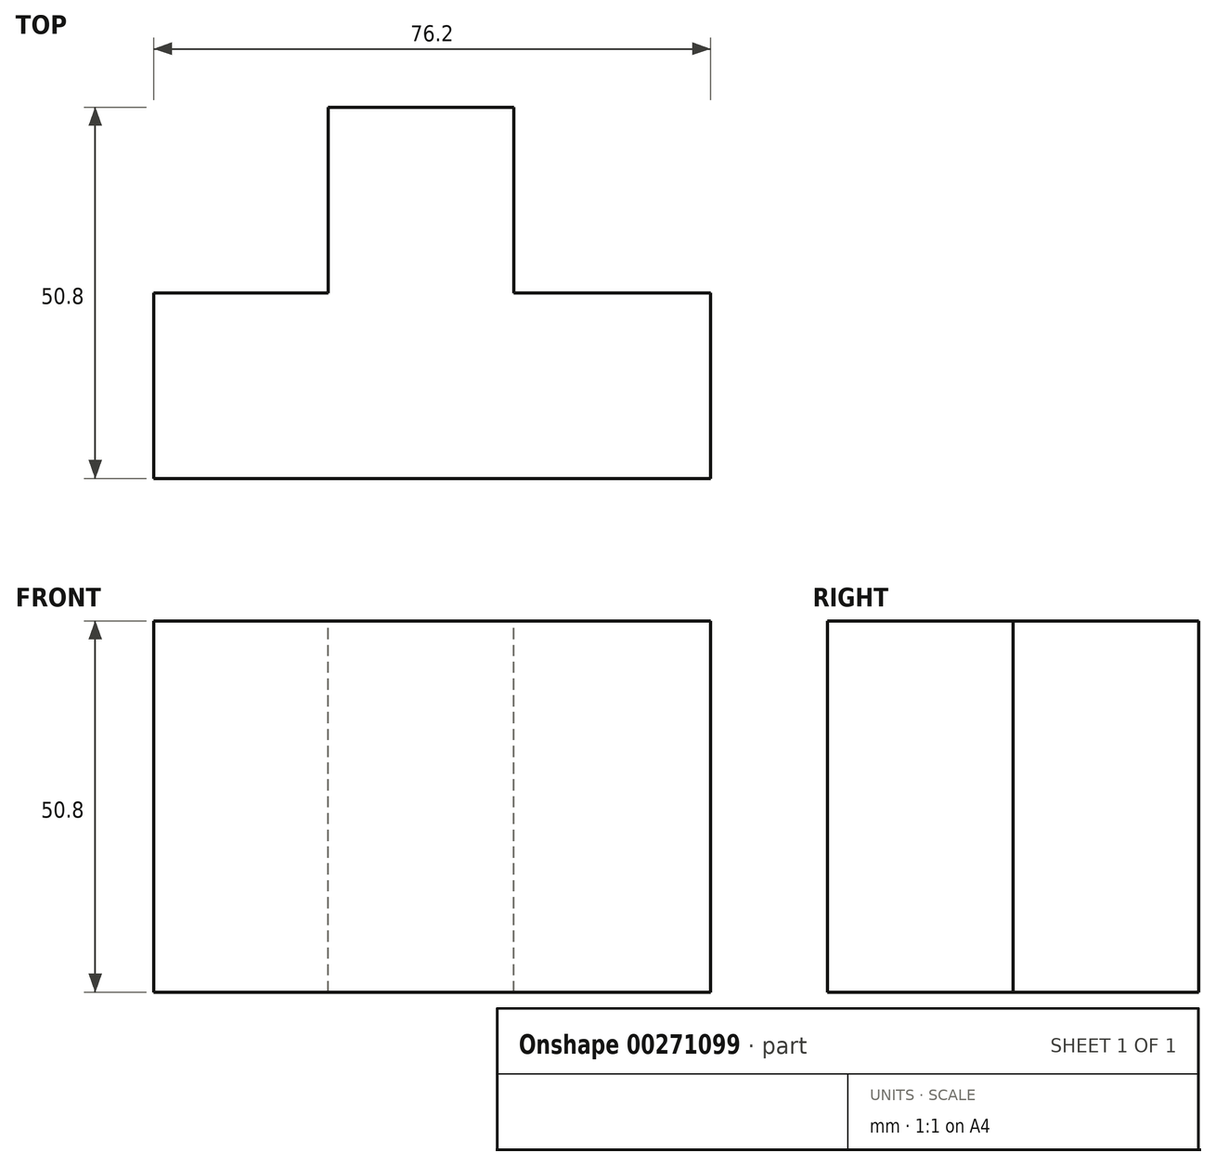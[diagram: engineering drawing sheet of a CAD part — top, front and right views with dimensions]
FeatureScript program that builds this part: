
annotation { "Feature Type Name" : "Feature", "Feature Type Description" : "" }
export const myFeature = defineFeature(function(context is Context, id is Id, definition is map)
    precondition{}
    {
        {
            var Q0;
            Q0=qCreatedBy(makeId("Front.planeOp"),FACE);
            var sketch = newSketch(context, id + "F0", { "sketchPlane" : qUnion([Q0])});
            skLineSegment(sketch, "E0.bottom", {"start": v(0, 0) * mm, "end": v(76.2, 0) * mm});
            skLineSegment(sketch, "E0.top", {"start": v(0, 50.8) * mm, "end": v(76.2, 50.8) * mm});
            skLineSegment(sketch, "E0.left", {"start": v(0, 0) * mm, "end": v(0, 50.8) * mm});
            skLineSegment(sketch, "E0.right", {"start": v(76.2, 0) * mm, "end": v(76.2, 50.8) * mm});
            skSolve(sketch);
        }
        {
            var Q0;
            Q0 = qSketchRegion(id + "F0", true);
            extrude(context, id + "F1", {"entities" : qUnion([Q0]), "depth" : 25.4 * mm});
        }
        {
            var Q0;
            Q0=qCreatedBy(makeId("Front.planeOp"),FACE);
            var sketch = newSketch(context, id + "F2", { "sketchPlane" : qUnion([Q0])});
            skLineSegment(sketch, "E1.bottom", {"start": v(23.85, 0) * mm, "end": v(49.25, 0) * mm});
            skLineSegment(sketch, "E1.top", {"start": v(23.85, 50.8) * mm, "end": v(49.25, 50.8) * mm});
            skLineSegment(sketch, "E1.left", {"start": v(23.85, 0) * mm, "end": v(23.85, 50.8) * mm});
            skLineSegment(sketch, "E1.right", {"start": v(49.25, 0) * mm, "end": v(49.25, 50.8) * mm});
            skSolve(sketch);
        }
        {
            var Q0;
            Q0=makeQuery(id+"F2.imprint","IMPRINT",FACE,{"disambiguationData":[TD([[makeQuery(id+"F2.imprint","IMPRINT",EDGE,{"derivedFrom":sQuery(id+"F2.wireOp",EDGE,"E1.bottom")}),1.0]])]});
            extrude(context, id + "F3", {"entities" : qUnion([Q0]), "operationType" : NewBodyOperationType.ADD, "oppositeDirection" : true, "depth" : 25.4 * mm});
        }
    });
